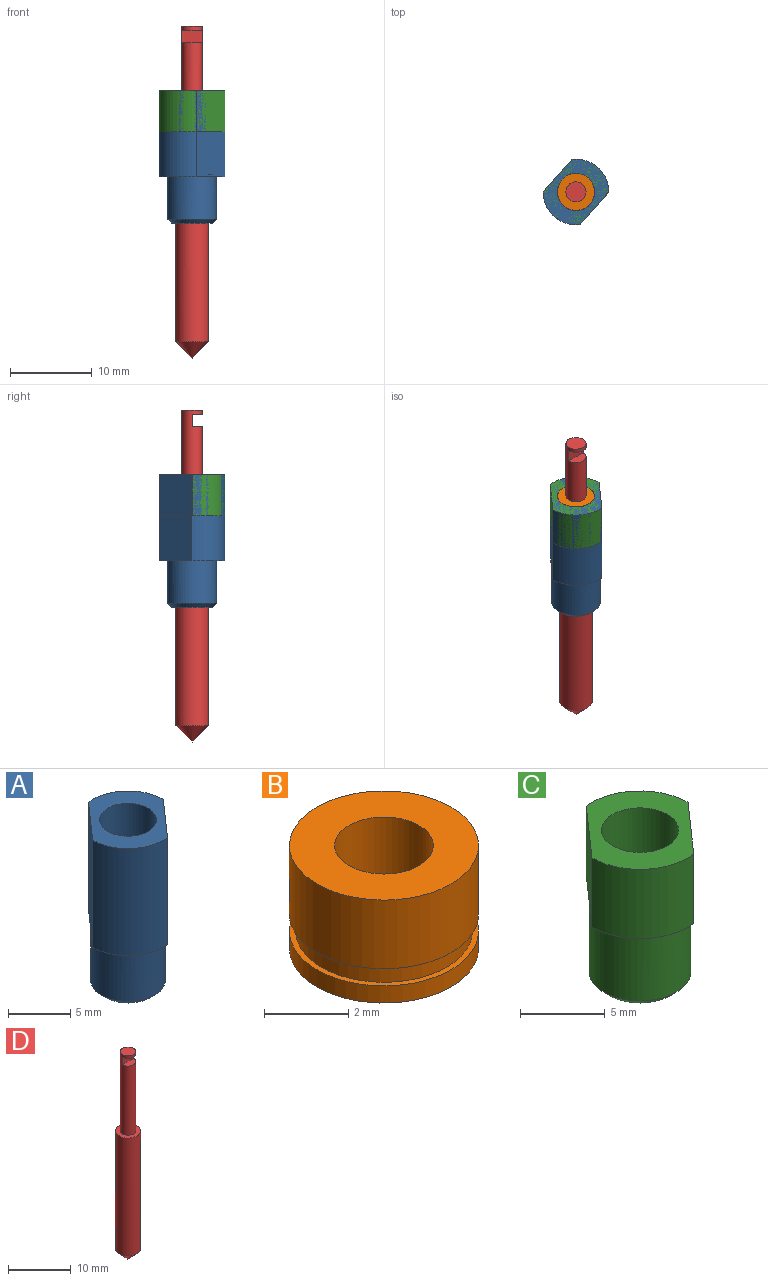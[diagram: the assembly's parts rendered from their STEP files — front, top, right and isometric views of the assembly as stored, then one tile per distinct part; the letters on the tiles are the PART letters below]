
ASSEMBLY  parts=4 mates=3
PART A: 11 faces, bbox 8x8x16.2 mm
  f0: cylinder r=4mm len=10.5mm, axis (0,0,-1), area 71.2mm2, adj f1,f2,f9,f10
  f1: plane 8x8mm, normal (0,0,1), area 26.8mm2, adj f0,f4,f5,f9,f10
  f2: plane 8x8mm, normal (0,0,-1), area 14.8mm2, adj f0,f5,f7,f9,f10
  f3: plane 4.99x4.99mm, normal (0,0,-1), area 3.3mm2, adj f4,f6
  f4: cylinder r=2.27mm len=10.5mm, axis (0,0,-1), area 150.1mm2, adj f1,f3
  f5: cylinder r=4mm len=10.5mm, axis (0,0,-1), area 71.2mm2, adj f1,f2,f9,f10
  f6: cylinder r=2.49mm len=5.7mm, axis (0,0,1), area 89.4mm2, adj f3,f8
  f7: cylinder r=2.99mm len=5.99mm, axis (0,0,1), area 97.9mm2, adj f2,f8
  f8: cone r=2.19mm half-angle=45deg, axis (0,0,1), area 12.2mm2, adj f6,f7
  f9: plane 10.5x3.97mm, normal (0.75,-0.66,0), area 55.6mm2, adj f0,f1,f2,f5
  f10: plane 10.5x3.97mm, normal (-0.75,0.66,0), area 55.6mm2, adj f0,f1,f2,f5
PART B: 8 faces, bbox 4.5x4.5x3 mm
  f0: cylinder r=1.18mm len=3mm, axis (0,0,-1), area 22.1mm2, adj f2,f6
  f1: cylinder r=2.25mm len=4.5mm, axis (0,0,-1), area 28.3mm2, adj f2,f3
  f2: plane 4.5x4.5mm, normal (0,0,1), area 11.6mm2, adj f0,f1
  f3: plane 4.5x4.5mm, normal (0,0,-1), area 2mm2, adj f1,f4
  f4: cylinder r=2.1mm len=4.2mm, axis (0,0,1), area 6.6mm2, adj f3,f7
  f5: cylinder r=2.25mm len=4.5mm, axis (0,0,1), area 7.1mm2, adj f6,f7
  f6: plane 4.5x4.5mm, normal (0,0,-1), area 11.6mm2, adj f0,f5
  f7: plane 4.5x4.5mm, normal (0,0,1), area 2mm2, adj f4,f5
PART C: 11 faces, bbox 8x8x10.7 mm
  f0: cylinder r=4mm len=5mm, axis (0,0,-1), area 33.9mm2, adj f1,f2,f9,f10
  f1: plane 8x8mm, normal (0,0,1), area 26.8mm2, adj f0,f4,f5,f9,f10
  f2: plane 8x8mm, normal (0,0,-1), area 14.8mm2, adj f0,f5,f7,f9,f10
  f3: plane 4.99x4.99mm, normal (0,0,-1), area 3.3mm2, adj f4,f6
  f4: cylinder r=2.27mm len=5mm, axis (0,0,-1), area 71.5mm2, adj f1,f3
  f5: cylinder r=4mm len=5mm, axis (0,0,-1), area 33.9mm2, adj f1,f2,f9,f10
  f6: cylinder r=2.49mm len=5.7mm, axis (0,0,1), area 89.4mm2, adj f3,f8
  f7: cylinder r=2.99mm len=5.99mm, axis (0,0,1), area 97.9mm2, adj f2,f8
  f8: cone r=2.19mm half-angle=45deg, axis (0,0,1), area 12.2mm2, adj f6,f7
  f9: plane 5x3.97mm, normal (0.75,-0.66,0), area 26.5mm2, adj f0,f1,f2,f5
  f10: plane 5x3.97mm, normal (-0.75,0.66,0), area 26.5mm2, adj f0,f1,f2,f5
PART D: 8 faces, bbox 4x4x40.5 mm
  f0: cylinder r=1.22mm len=15.5mm, axis (0,0,-1), area 113.5mm2, adj f1,f3,f5,f6,f7
  f1: plane 2.45x1.23mm, normal (0,0,1), area 2.4mm2, adj f0,f5
  f2: cylinder r=2mm len=23mm, axis (0,0,1), area 289mm2, adj f3,f4
  f3: plane 4x4mm, normal (0,0,1), area 7.9mm2, adj f0,f2
  f4: cone r=2mm half-angle=45deg, axis (0,0,1), area 17.8mm2, adj f2
  f5: plane 2.45x1.5mm, normal (0,-1,0), area 3.7mm2, adj f0,f1,f6
  f6: plane 2.45x1.23mm, normal (0,0,-1), area 2.4mm2, adj f0,f5
  f7: plane 2.45x2.45mm, normal (0,0,1), area 4.7mm2, adj f0
PLACE A t=(-4.25,-5.3,-2.26)mm
PLACE B t=(-4.25,-5.3,6.24)mm
PLACE C t=(-4.25,-5.3,3.24)mm
PLACE D t=(-4.25,-5.3,0.62)mm
MATE planar C.f0 <-> B.f1  axis (0,0,1) through (-4.25,-5.3,8.24)mm
MATE slider B.f0 <-> D.f0  axis (0,0,-1) through (-4.25,-5.3,8.24)mm
MATE slider C.f4 <-> B.f1  axis (0,0,-1) through (-4.25,-5.3,8.24)mm
